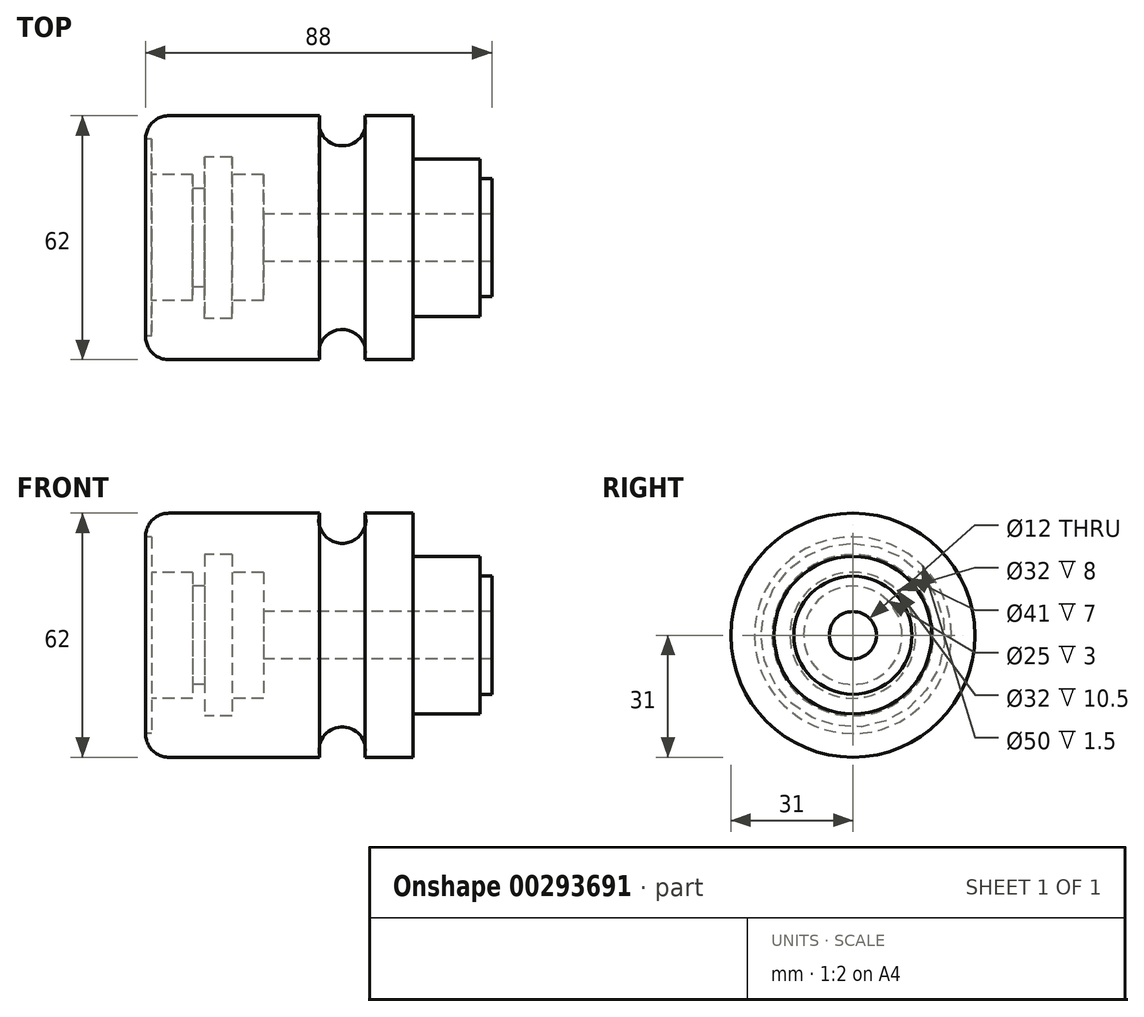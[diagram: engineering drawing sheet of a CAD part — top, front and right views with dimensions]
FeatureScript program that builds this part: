
annotation { "Feature Type Name" : "Feature", "Feature Type Description" : "" }
export const myFeature = defineFeature(function(context is Context, id is Id, definition is map)
    precondition{}
    {
        {
            var Q0;
            Q0=qCreatedBy(makeId("Front.planeOp"),FACE);
            var sketch = newSketch(context, id + "F0", { "sketchPlane" : qUnion([Q0])});
            skLineSegment(sketch, "E0", {"start": v(0, 0) * mm, "end": v(171.93, 0) * mm, "construction": true});
            skLineSegment(sketch, "E1", {"start": v(0, 0) * mm, "end": v(0, 31) * mm});
            skLineSegment(sketch, "E2", {"start": v(0, 31) * mm, "end": v(44.23, 31) * mm});
            skLineSegment(sketch, "E3", {"start": v(68, 31) * mm, "end": v(68, 20) * mm});
            skLineSegment(sketch, "E4", {"start": v(68, 20) * mm, "end": v(85, 20) * mm});
            skLineSegment(sketch, "E5", {"start": v(85, 20) * mm, "end": v(85, 15) * mm});
            skLineSegment(sketch, "E6", {"start": v(85, 15) * mm, "end": v(88, 15) * mm});
            skLineSegment(sketch, "E7", {"start": v(88, 15) * mm, "end": v(88, 0) * mm});
            skLineSegment(sketch, "E8", {"start": v(88, 0) * mm, "end": v(0, 0) * mm});
            skArc(sketch, "E9", {"start": v(44.23, 31) * mm, "mid": v(50, 23.34) * mm, "end": v(55.77, 31) * mm});
            skLineSegment(sketch, "E10.trimOffspring", {"start": v(55.77, 31) * mm, "end": v(68, 31) * mm});
            skSolve(sketch);
        }
        {
            var Q0;
            Q0=makeQuery(id+"F0.imprint","IMPRINT",FACE,{"disambiguationData":[TD([[makeQuery(id+"F0.imprint","IMPRINT",EDGE,{"derivedFrom":sQuery(id+"F0.wireOp",EDGE,"E1")}),-1.0]])]});
            var Q1;
            Q1=sQuery(id+"F0.wireOp",EDGE,"E0");
            revolve(context, id + "F1", {"entities" : qUnion([Q0]), "axis" : qUnion([Q1]), "revolveType" : RevolveType.FULL});
        }
        {
            var Q0;
            Q0=qCreatedBy(makeId("Front.planeOp"),FACE);
            var sketch = newSketch(context, id + "F2", { "sketchPlane" : qUnion([Q0])});
            skLineSegment(sketch, "E11", {"start": v(0, 0) * mm, "end": v(0, 25) * mm});
            skLineSegment(sketch, "E12", {"start": v(0, 25) * mm, "end": v(1.5, 25) * mm});
            skLineSegment(sketch, "E13", {"start": v(1.5, 25) * mm, "end": v(1.5, 16) * mm});
            skLineSegment(sketch, "E14", {"start": v(1.5, 16) * mm, "end": v(12, 16) * mm});
            skLineSegment(sketch, "E15", {"start": v(12, 16) * mm, "end": v(12, 12.5) * mm});
            skLineSegment(sketch, "E16", {"start": v(12, 12.5) * mm, "end": v(15, 12.5) * mm});
            skLineSegment(sketch, "E17", {"start": v(15, 12.5) * mm, "end": v(15, 20.5) * mm});
            skLineSegment(sketch, "E18", {"start": v(15, 20.5) * mm, "end": v(22, 20.5) * mm});
            skLineSegment(sketch, "E19", {"start": v(22, 20.5) * mm, "end": v(22, 16) * mm});
            skLineSegment(sketch, "E20", {"start": v(22, 16) * mm, "end": v(30, 16) * mm});
            skLineSegment(sketch, "E21", {"start": v(30, 16) * mm, "end": v(30, 12.5) * mm});
            skLineSegment(sketch, "E22", {"start": v(88, 6) * mm, "end": v(88, 0) * mm});
            skLineSegment(sketch, "E23", {"start": v(88, 0) * mm, "end": v(0, 0) * mm});
            skLineSegment(sketch, "E24", {"start": v(0, 0) * mm, "end": v(-20.9, 0) * mm, "construction": true});
            skLineSegment(sketch, "E25", {"start": v(30, 12.5) * mm, "end": v(30, 6) * mm});
            skLineSegment(sketch, "E26", {"start": v(30, 6) * mm, "end": v(88, 6) * mm});
            skSolve(sketch);
        }
        {
            var Q0;
            Q0 = qSketchRegion(id + "F2", true);
            var Q1;
            Q1=sQuery(id+"F2.wireOp",EDGE,"E24");
            revolve(context, id + "F3", {"operationType" : NewBodyOperationType.REMOVE, "entities" : qUnion([Q0]), "axis" : qUnion([Q1]), "revolveType" : RevolveType.FULL, "oppositeDirection" : true});
        }
        {
            var Q0;
            Q0=makeQuery(id+"F1.opRevolve","SWEPT_EDGE",EDGE,{"disambiguationData":[OSD([sQuery(id+"F0.wireOp",EDGE,"E1"),sQuery(id+"F0.wireOp",EDGE,"E2")])]});
            fillet(context, id + "F4", {"entities" : qUnion([Q0]), "radius" : 6 * mm, "tangentPropagation" : true, "allowEdgeOverflow" : false});
        }
    });
